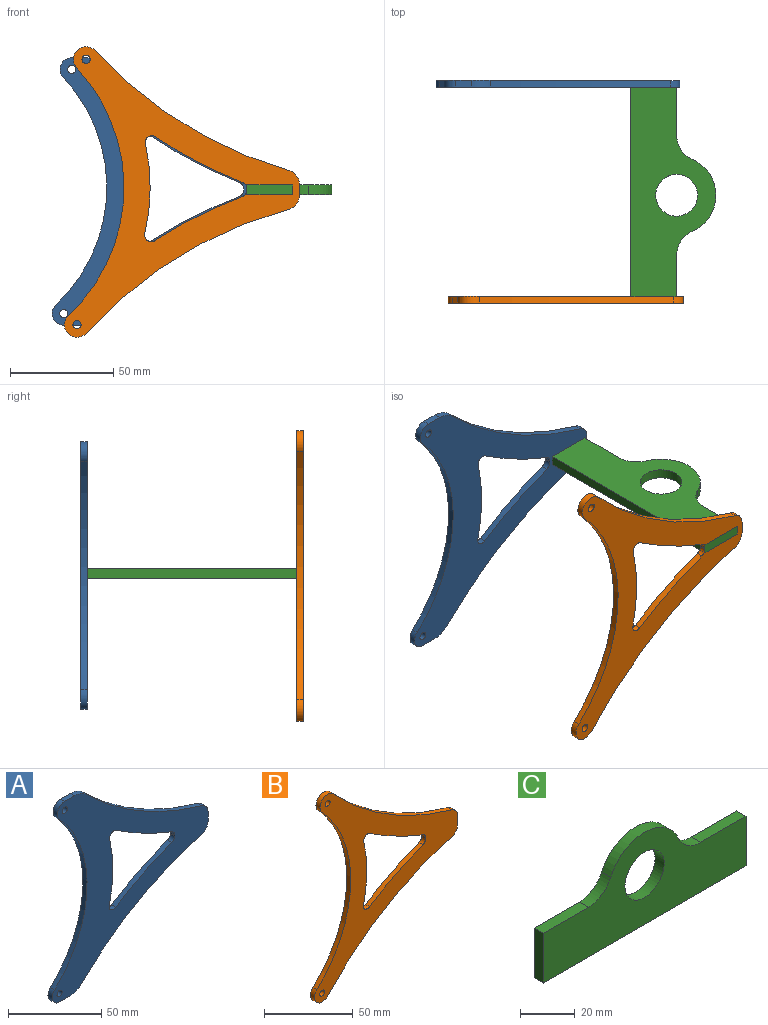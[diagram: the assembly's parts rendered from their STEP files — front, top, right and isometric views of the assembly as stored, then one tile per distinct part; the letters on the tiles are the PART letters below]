
ASSEMBLY  parts=3 mates=2
PART A: 24 faces, bbox 118.2x3.2x129.7 mm
  f0: cylinder r=3.17mm len=3.18mm, axis (0,1,0), area 12.3mm2, adj f1,f21,f22,f23
  f1: cylinder r=215.9mm len=42.54mm, axis (0,1,0), area 151.5mm2, adj f0,f2,f22,f23
  f2: cylinder r=3.17mm len=4.91mm, axis (0,1,0), area 24mm2, adj f1,f3,f22,f23
  f3: cylinder r=97.61mm len=43.61mm, axis (0,1,0), area 139.7mm2, adj f2,f4,f22,f23
  f4: cylinder r=3.17mm len=4.95mm, axis (0,1,0), area 24mm2, adj f3,f5,f22,f23
  f5: cylinder r=215.9mm len=42.27mm, axis (0,1,0), area 151.8mm2, adj f4,f6,f22,f23
  f6: cylinder r=3.17mm len=3.18mm, axis (0,1,0), area 12.1mm2, adj f5,f21,f22,f23
  f7: plane 7.68x3.18mm, normal (0,0,1), area 24.4mm2, adj f8,f18,f22,f23
  f8: cylinder r=5.66mm len=9.53mm, axis (0,1,0), area 41.7mm2, adj f7,f9,f22,f23
  f9: cylinder r=78.13mm len=110.44mm, axis (0,1,0), area 389.7mm2, adj f8,f10,f22,f23
  f10: cylinder r=5.64mm len=9.75mm, axis (0,1,0), area 42.7mm2, adj f9,f11,f22,f23
  f11: plane 7.62x3.18mm, normal (0,0,-1), area 24.2mm2, adj f10,f12,f22,f23
  f12: cylinder r=12.7mm len=8.98mm, axis (0,1,0), area 31.6mm2, adj f11,f13,f22,f23
  f13: cylinder r=203.2mm len=91.25mm, axis (0,1,0), area 338.2mm2, adj f12,f14,f22,f23
  f14: cylinder r=6.35mm len=6.14mm, axis (0,1,0), area 26.4mm2, adj f13,f15,f22,f23
  f15: plane 6.35x3.18mm, normal (1,0,0), area 20.2mm2, adj f14,f16,f22,f23
  f16: cylinder r=6.35mm len=6.11mm, axis (0,1,0), area 26.1mm2, adj f15,f17,f22,f23
  f17: cylinder r=203.2mm len=87.47mm, axis (0,1,0), area 325.1mm2, adj f16,f18,f22,f23
  f18: cylinder r=12.7mm len=8.94mm, axis (0,1,0), area 31.5mm2, adj f7,f17,f22,f23
  f19: cylinder r=1.98mm len=3.96mm, axis (0,1,0), area 39.5mm2, adj f22,f23
  f20: cylinder r=1.98mm len=3.96mm, axis (0,1,0), area 39.5mm2, adj f22,f23
  f21: plane 3.18x0.87mm, normal (-1,0,0), area 2.8mm2, adj f0,f6,f22,f23
  f22: plane 129.71x118.2mm, normal (0,-1,0), area 5029.9mm2, adj f0,f1,f2,f3,f4,f5,f6,f7
  f23: plane 129.71x118.2mm, normal (0,1,0), area 5029.9mm2, adj f0,f1,f2,f3,f4,f5,f6,f7
PART B: 20 faces, bbox 113.8x3.2x140.9 mm
  f0: cylinder r=203.2mm len=94.2mm, axis (0,1,0), area 356mm2, adj f1,f17,f18,f19
  f1: cylinder r=6.12mm len=10.63mm, axis (0,1,0), area 61.2mm2, adj f0,f2,f18,f19
  f2: cylinder r=84.91mm len=120.01mm, axis (0,1,0), area 423.5mm2, adj f1,f3,f18,f19
  f3: cylinder r=6.12mm len=10.66mm, axis (0,1,0), area 62.7mm2, adj f2,f4,f18,f19
  f4: cylinder r=203.2mm len=98.45mm, axis (0,1,0), area 371.4mm2, adj f3,f5,f18,f19
  f5: cylinder r=6.35mm len=6.14mm, axis (0,1,0), area 26.4mm2, adj f4,f6,f18,f19
  f6: plane 6.35x3.18mm, normal (1,0,0), area 20.2mm2, adj f5,f17,f18,f19
  f7: cylinder r=3.17mm len=4.95mm, axis (0,1,0), area 24mm2, adj f8,f14,f18,f19
  f8: cylinder r=215.9mm len=42.27mm, axis (0,1,0), area 151.8mm2, adj f7,f9,f18,f19
  f9: cylinder r=3.17mm len=3.18mm, axis (0,1,0), area 12.1mm2, adj f8,f10,f18,f19
  f10: plane 3.18x0.87mm, normal (-1,0,0), area 2.8mm2, adj f9,f11,f18,f19
  f11: cylinder r=3.17mm len=3.18mm, axis (0,1,0), area 12.3mm2, adj f10,f12,f18,f19
  f12: cylinder r=215.9mm len=42.54mm, axis (0,1,0), area 151.5mm2, adj f11,f13,f18,f19
  f13: cylinder r=3.17mm len=4.91mm, axis (0,1,0), area 24mm2, adj f12,f14,f18,f19
  f14: cylinder r=97.61mm len=43.61mm, axis (0,1,0), area 139.7mm2, adj f7,f13,f18,f19
  f15: cylinder r=1.98mm len=3.96mm, axis (0,1,0), area 39.5mm2, adj f18,f19
  f16: cylinder r=1.98mm len=3.96mm, axis (0,1,0), area 39.5mm2, adj f18,f19
  f17: cylinder r=6.35mm len=6.11mm, axis (0,1,0), area 26.1mm2, adj f0,f6,f18,f19
  f18: plane 140.89x113.82mm, normal (0,-1,0), area 4207.7mm2, adj f0,f1,f2,f3,f4,f5,f6,f7
  f19: plane 140.89x113.82mm, normal (0,1,0), area 4207.7mm2, adj f0,f1,f2,f3,f4,f5,f6,f7
PART C: 11 faces, bbox 104.8x4.8x41.3 mm
  f0: plane 22.23x4.75mm, normal (1,0,0), area 105.6mm2, adj f1,f8,f9,f10
  f1: plane 23.29x4.75mm, normal (0,0,1), area 110.6mm2, adj f0,f2,f9,f10
  f2: cylinder r=12.7mm len=11.64mm, axis (0,1,0), area 69.9mm2, adj f1,f3,f9,f10
  f3: cylinder r=19.05mm len=34.92mm, axis (0,1,0), area 209.8mm2, adj f2,f4,f9,f10
  f4: cylinder r=12.7mm len=11.64mm, axis (0,1,0), area 69.9mm2, adj f3,f5,f9,f10
  f5: plane 23.29x4.75mm, normal (0,0,1), area 110.6mm2, adj f4,f6,f9,f10
  f6: plane 22.23x4.75mm, normal (-1,0,0), area 105.6mm2, adj f5,f8,f9,f10
  f7: cylinder r=10.16mm len=20.32mm, axis (0,1,0), area 303.2mm2, adj f9,f10
  f8: plane 104.78x4.75mm, normal (0,0,-1), area 497.7mm2, adj f0,f6,f9,f10
  f9: plane 104.78x41.28mm, normal (0,-1,0), area 2607.6mm2, adj f0,f1,f2,f3,f4,f5,f6,f7
  f10: plane 104.78x41.28mm, normal (0,1,0), area 2607.6mm2, adj f0,f1,f2,f3,f4,f5,f6,f7
PLACE A t=(-94.52,-240.21,35.29)mm
PLACE B t=(-198.59,-344.98,114.94)mm
PLACE C rot(axis=(0.58,0.58,0.58),120deg) t=(-207.51,-528.81,67.9)mm
MATE fastened B.f18 <-> C.f6  axis (0,-1,0) through (-81.43,-348.16,65.53)mm
MATE fastened C.f0 <-> A.f22  axis (0,1,0) through (-82.99,-243.38,65.53)mm
